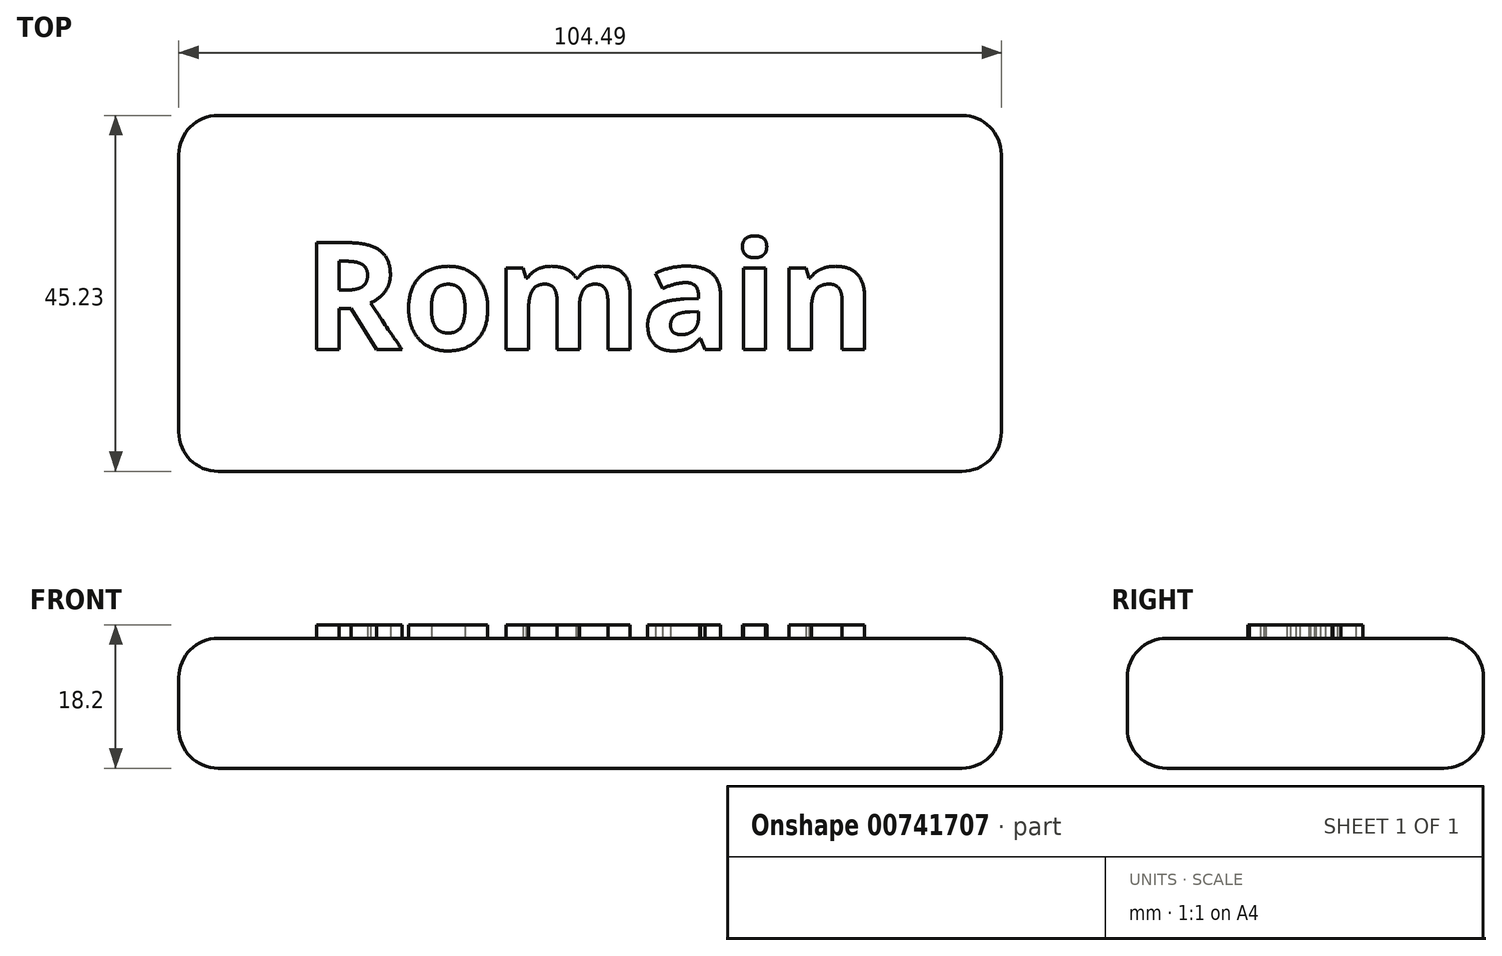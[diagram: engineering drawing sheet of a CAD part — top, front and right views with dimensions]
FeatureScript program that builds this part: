
annotation { "Feature Type Name" : "Feature", "Feature Type Description" : "" }
export const myFeature = defineFeature(function(context is Context, id is Id, definition is map)
    precondition{}
    {
        {
            var Q0;
            Q0=qCreatedBy(makeId("Top.planeOp"),FACE);
            var sketch = newSketch(context, id + "F0", { "sketchPlane" : qUnion([Q0])});
            skLineSegment(sketch, "E0.bottom", {"start": v(47.67, 13.9) * mm, "end": v(-46.82, 13.9) * mm});
            skLineSegment(sketch, "E0.top", {"start": v(47.67, -31.32) * mm, "end": v(-46.82, -31.32) * mm});
            skLineSegment(sketch, "E0.left", {"start": v(52.67, 8.9) * mm, "end": v(52.67, -26.32) * mm});
            skLineSegment(sketch, "E0.right", {"start": v(-51.82, 8.9) * mm, "end": v(-51.82, -26.32) * mm});
            skPoint(sketch, "E1.visualSharp", {"position": v(-51.82, 13.9) * mm});
            skArc(sketch, "E1.filletArc", {"start": v(-46.82, 13.9) * mm, "mid": v(-50.35, 12.44) * mm, "end": v(-51.82, 8.9) * mm});
            skPoint(sketch, "E2.visualSharp", {"position": v(-51.82, -31.32) * mm});
            skArc(sketch, "E2.filletArc", {"start": v(-51.82, -26.32) * mm, "mid": v(-50.35, -29.86) * mm, "end": v(-46.82, -31.32) * mm});
            skPoint(sketch, "E3.visualSharp", {"position": v(52.67, -31.32) * mm});
            skArc(sketch, "E3.filletArc", {"start": v(47.67, -31.32) * mm, "mid": v(51.2, -29.86) * mm, "end": v(52.67, -26.32) * mm});
            skPoint(sketch, "E4.visualSharp", {"position": v(52.67, 13.9) * mm});
            skArc(sketch, "E4.filletArc", {"start": v(52.67, 8.9) * mm, "mid": v(51.2, 12.44) * mm, "end": v(47.67, 13.9) * mm});
            skSolve(sketch);
        }
        {
            var Q0;
            Q0=qCreatedBy(makeId("Top.planeOp"),FACE);
            var sketch = newSketch(context, id + "F1", { "sketchPlane" : qUnion([Q0])});
            skText(sketch, "E5", { "text": "Romain", "fontName": "OpenSans-Bold.ttf"});
            const initialGuessF1  = {"E5": [-0.03602, -0.01583, 1, 0, 0.01368]};
            skSetInitialGuess(sketch, initialGuessF1);
            skSolve(sketch);
        }
        {
            var Q0;
            Q0=makeQuery(id+"F0.imprint","IMPRINT",FACE,{"disambiguationData":[TD([[makeQuery(id+"F0.imprint","IMPRINT",EDGE,{"derivedFrom":sQuery(id+"F0.wireOp",EDGE,"E0.bottom")}),1.0]])]});
            extrude(context, id + "F2", {"entities" : qUnion([Q0]), "depth" : 16.5 * mm, "offsetDistance" : 25 * mm});
        }
        {
            var Q0;
            Q0 = qSketchRegion(id + "F1", true);
            extrude(context, id + "F3", {"entities" : qUnion([Q0]), "operationType" : NewBodyOperationType.ADD, "depth" : 18.2 * mm, "offsetDistance" : 25 * mm});
        }
        {
            var Q0;
            Q0=makeQuery(id+"F2.opExtrude","CAP_EDGE",EDGE,{"disambiguationData":[OSD([sQuery(id+"F0.wireOp",EDGE,"E0.top")])],"isStart":false});
            var Q1;
            Q1=makeQuery(id+"F2.opExtrude","CAP_EDGE",EDGE,{"disambiguationData":[OSD([sQuery(id+"F0.wireOp",EDGE,"E0.top")])],"isStart":true});
            fillet(context, id + "F4", {"entities" : qUnion([Q0, Q1]), "radius" : 5 * mm, "tangentPropagation" : true, "allowEdgeOverflow" : false});
        }
    });
